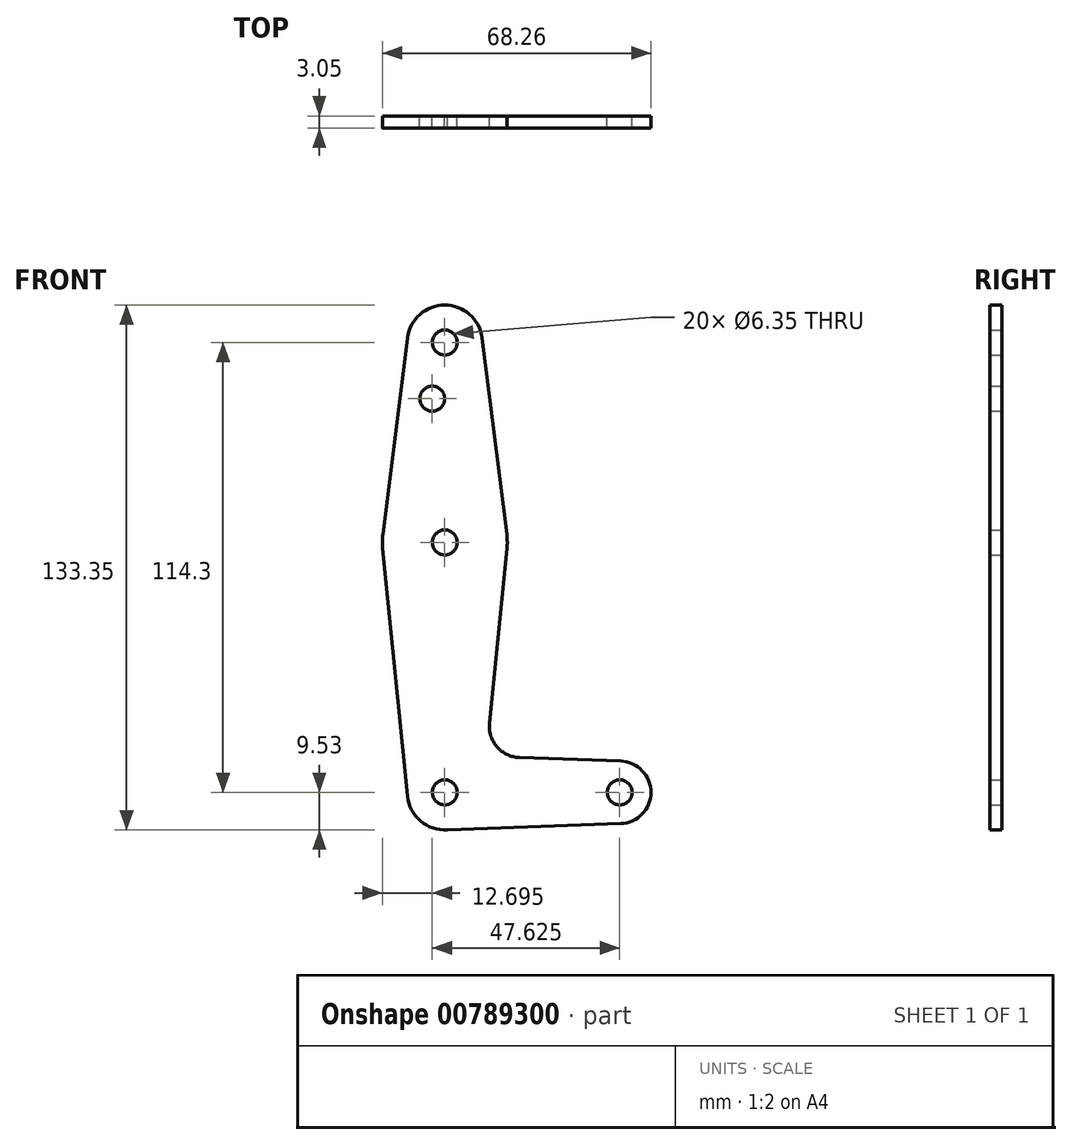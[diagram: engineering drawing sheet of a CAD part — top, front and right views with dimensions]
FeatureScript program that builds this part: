
annotation { "Feature Type Name" : "Feature", "Feature Type Description" : "" }
export const myFeature = defineFeature(function(context is Context, id is Id, definition is map)
    precondition{}
    {
        {
            var Q0;
            Q0=qCreatedBy(makeId("Front.planeOp"),FACE);
            var sketch = newSketch(context, id + "F0", { "sketchPlane" : qUnion([Q0])});
            skCircle(sketch, "E0", {"center": v(0, 0) * mm, "radius": 15.88 * mm});
            skCircle(sketch, "E1", {"center": v(0, 50.8) * mm, "radius": 9.53 * mm});
            skCircle(sketch, "E2", {"center": v(0, -63.5) * mm, "radius": 9.53 * mm});
            skCircle(sketch, "E3", {"center": v(44.45, -63.5) * mm, "radius": 7.94 * mm});
            skCircle(sketch, "E4", {"center": v(0, 50.8) * mm, "radius": 3.18 * mm});
            skCircle(sketch, "E5", {"center": v(0, 0) * mm, "radius": 3.18 * mm});
            skCircle(sketch, "E6", {"center": v(0, -63.5) * mm, "radius": 3.18 * mm});
            skCircle(sketch, "E7", {"center": v(44.45, -63.5) * mm, "radius": 3.18 * mm});
            skCircle(sketch, "E8", {"center": v(-3.18, 36.53) * mm, "radius": 3.18 * mm});
            skLineSegment(sketch, "E9", {"start": v(-9.45, 52) * mm, "end": v(-15.75, 1.98) * mm});
            skLineSegment(sketch, "E10", {"start": v(-15.8, -1.59) * mm, "end": v(-9.48, -64.45) * mm});
            skLineSegment(sketch, "E11", {"start": v(9.45, 52) * mm, "end": v(15.75, 1.98) * mm});
            skLineSegment(sketch, "E12", {"start": v(15.8, -1.59) * mm, "end": v(11.34, -45.91) * mm});
            skLineSegment(sketch, "E13", {"start": v(18.97, -54.65) * mm, "end": v(44.73, -55.57) * mm});
            skLineSegment(sketch, "E14", {"start": v(0, -73.02) * mm, "end": v(44.73, -71.43) * mm});
            skPoint(sketch, "E15.newPointB", {"position": v(0, -53.97) * mm});
            skArc(sketch, "E15.filletArc", {"start": v(11.34, -45.91) * mm, "mid": v(13.26, -51.93) * mm, "end": v(18.97, -54.65) * mm});
            skSolve(sketch);
        }
        {
            var Q0;
            Q0 = qSketchRegion(id + "F0", true);
            extrude(context, id + "F1", {"entities" : qUnion([Q0]), "depth" : 3.05 * mm, "offsetDistance" : 25.4 * mm});
        }
    });
